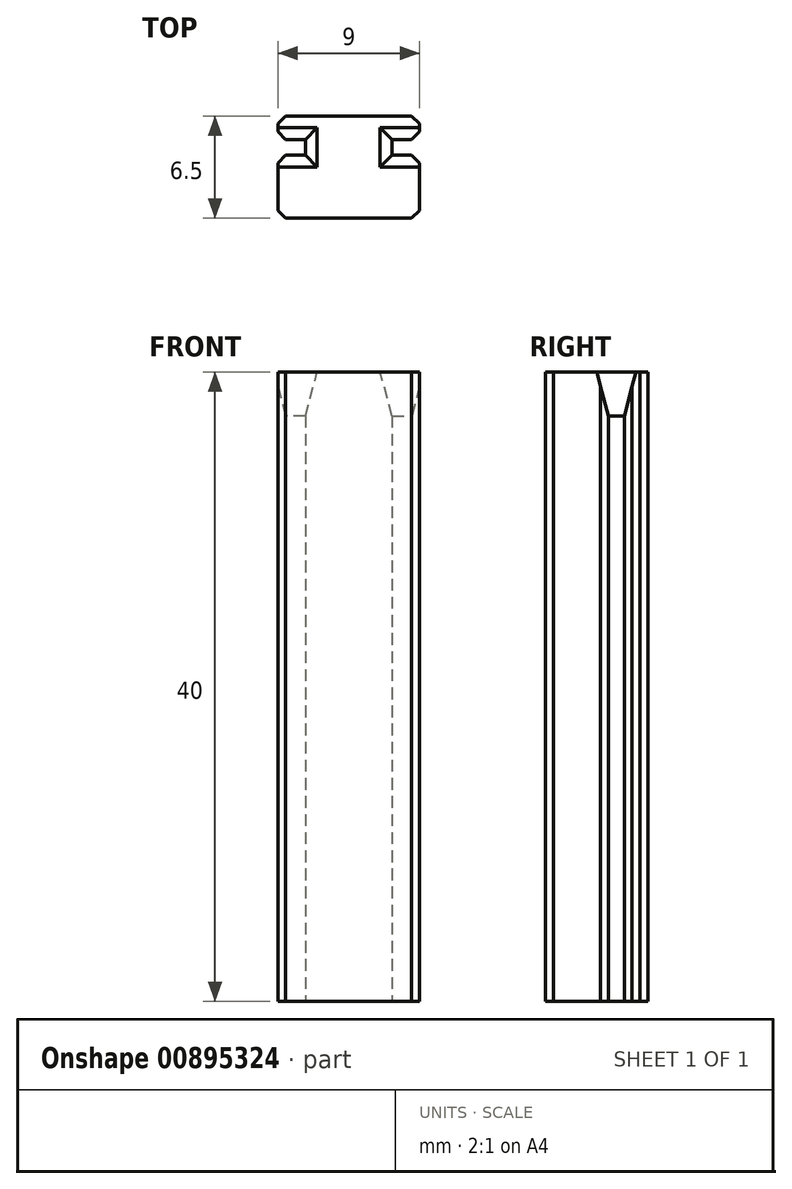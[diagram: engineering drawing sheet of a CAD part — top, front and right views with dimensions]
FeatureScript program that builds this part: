
annotation { "Feature Type Name" : "Feature", "Feature Type Description" : "" }
export const myFeature = defineFeature(function(context is Context, id is Id, definition is map)
    precondition{}
    {
        {
            var Q0;
            Q0=qCreatedBy(makeId("Top.planeOp"),FACE);
            var sketch = newSketch(context, id + "F0", { "sketchPlane" : qUnion([Q0])});
            skLineSegment(sketch, "E0", {"start": v(-4.5, 0) * mm, "end": v(4.5, 0) * mm});
            skLineSegment(sketch, "E1", {"start": v(4.5, 0) * mm, "end": v(4.5, 4) * mm});
            skLineSegment(sketch, "E2", {"start": v(4.5, 4) * mm, "end": v(2.75, 4) * mm});
            skLineSegment(sketch, "E3", {"start": v(2.75, 4) * mm, "end": v(2.75, 5) * mm});
            skLineSegment(sketch, "E4", {"start": v(2.75, 5) * mm, "end": v(4.5, 5) * mm});
            skLineSegment(sketch, "E5", {"start": v(4.5, 5) * mm, "end": v(4.5, 6.5) * mm});
            skLineSegment(sketch, "E6", {"start": v(4.5, 6.5) * mm, "end": v(-4.5, 6.5) * mm});
            skLineSegment(sketch, "E7", {"start": v(-4.5, 6.5) * mm, "end": v(-4.5, 5) * mm});
            skLineSegment(sketch, "E8", {"start": v(-4.5, 5) * mm, "end": v(-2.75, 5) * mm});
            skLineSegment(sketch, "E9", {"start": v(-2.75, 5) * mm, "end": v(-2.75, 4) * mm});
            skLineSegment(sketch, "E10", {"start": v(-2.75, 4) * mm, "end": v(-4.5, 4) * mm});
            skLineSegment(sketch, "E11", {"start": v(-4.5, 4) * mm, "end": v(-4.5, 0) * mm});
            skSolve(sketch);
        }
        {
            var Q0;
            Q0=makeQuery(id+"F0.imprint","IMPRINT",FACE,{"disambiguationData":[TD([[makeQuery(id+"F0.imprint","IMPRINT",EDGE,{"derivedFrom":sQuery(id+"F0.wireOp",EDGE,"E0")}),1.0]])]});
            extrude(context, id + "F1", {"entities" : qUnion([Q0]), "depth" : 40 * mm, "offsetDistance" : 25 * mm});
        }
        {
            var Q0;
            Q0=makeQuery(id+"F1.opExtrude","SWEPT_EDGE",EDGE,{"disambiguationData":[OSD([sQuery(id+"F0.wireOp",EDGE,"E7"),sQuery(id+"F0.wireOp",EDGE,"E8")])]});
            var Q1;
            Q1=makeQuery(id+"F1.opExtrude","SWEPT_EDGE",EDGE,{"disambiguationData":[OSD([sQuery(id+"F0.wireOp",EDGE,"E10"),sQuery(id+"F0.wireOp",EDGE,"E11")])]});
            var Q2;
            Q2=makeQuery(id+"F1.opExtrude","SWEPT_EDGE",EDGE,{"disambiguationData":[OSD([sQuery(id+"F0.wireOp",EDGE,"E1"),sQuery(id+"F0.wireOp",EDGE,"E2")])]});
            var Q3;
            Q3=makeQuery(id+"F1.opExtrude","SWEPT_EDGE",EDGE,{"disambiguationData":[OSD([sQuery(id+"F0.wireOp",EDGE,"E4"),sQuery(id+"F0.wireOp",EDGE,"E5")])]});
            var Q4;
            Q4=makeQuery(id+"F1.opExtrude","SWEPT_EDGE",EDGE,{"disambiguationData":[OSD([sQuery(id+"F0.wireOp",EDGE,"E5"),sQuery(id+"F0.wireOp",EDGE,"E6")])]});
            var Q5;
            Q5=makeQuery(id+"F1.opExtrude","SWEPT_EDGE",EDGE,{"disambiguationData":[OSD([sQuery(id+"F0.wireOp",EDGE,"E0"),sQuery(id+"F0.wireOp",EDGE,"E1")])]});
            var Q6;
            Q6=makeQuery(id+"F1.opExtrude","SWEPT_EDGE",EDGE,{"disambiguationData":[OSD([sQuery(id+"F0.wireOp",EDGE,"E6"),sQuery(id+"F0.wireOp",EDGE,"E7")])]});
            var Q7;
            Q7=makeQuery(id+"F1.opExtrude","SWEPT_EDGE",EDGE,{"disambiguationData":[OSD([sQuery(id+"F0.wireOp",EDGE,"E0"),sQuery(id+"F0.wireOp",EDGE,"E11")])]});
            chamfer(context, id + "F2", {"entities" : qUnion([Q0, Q1, Q2, Q3, Q4, Q5, Q6, Q7]), "width" : .5 * mm, "tangentPropagation" : true});
        }
        {
            var Q0;
            Q0=makeQuery(id+"F1.opExtrude","CAP_EDGE",EDGE,{"disambiguationData":[OSD([sQuery(id+"F0.wireOp",EDGE,"E9")])],"isStart":false});
            var Q1;
            Q1=makeQuery(id+"F1.opExtrude","CAP_EDGE",EDGE,{"disambiguationData":[OSD([sQuery(id+"F0.wireOp",EDGE,"E3")])],"isStart":false});
            var Q2;
            Q2=makeQuery(id+"F1.opExtrude","CAP_EDGE",EDGE,{"disambiguationData":[OSD([sQuery(id+"F0.wireOp",EDGE,"E10")])],"isStart":false});
            var Q3;
            Q3=makeQuery(id+"F1.opExtrude","CAP_EDGE",EDGE,{"disambiguationData":[OSD([sQuery(id+"F0.wireOp",EDGE,"E8")])],"isStart":false});
            var Q4;
            Q4=makeQuery(id+"F1.opExtrude","CAP_EDGE",EDGE,{"disambiguationData":[OSD([sQuery(id+"F0.wireOp",EDGE,"E4")])],"isStart":false});
            var Q5;
            Q5=makeQuery(id+"F1.opExtrude","CAP_EDGE",EDGE,{"disambiguationData":[OSD([sQuery(id+"F0.wireOp",EDGE,"E2")])],"isStart":false});
            chamfer(context, id + "F3", {"entities" : qUnion([Q0, Q1, Q2, Q3, Q4, Q5]), "chamferType" : ChamferType.OFFSET_ANGLE, "width" : .75 * mm, "oppositeDirection" : false, "angle" : 75 * degree, "tangentPropagation" : true});
        }
    });
